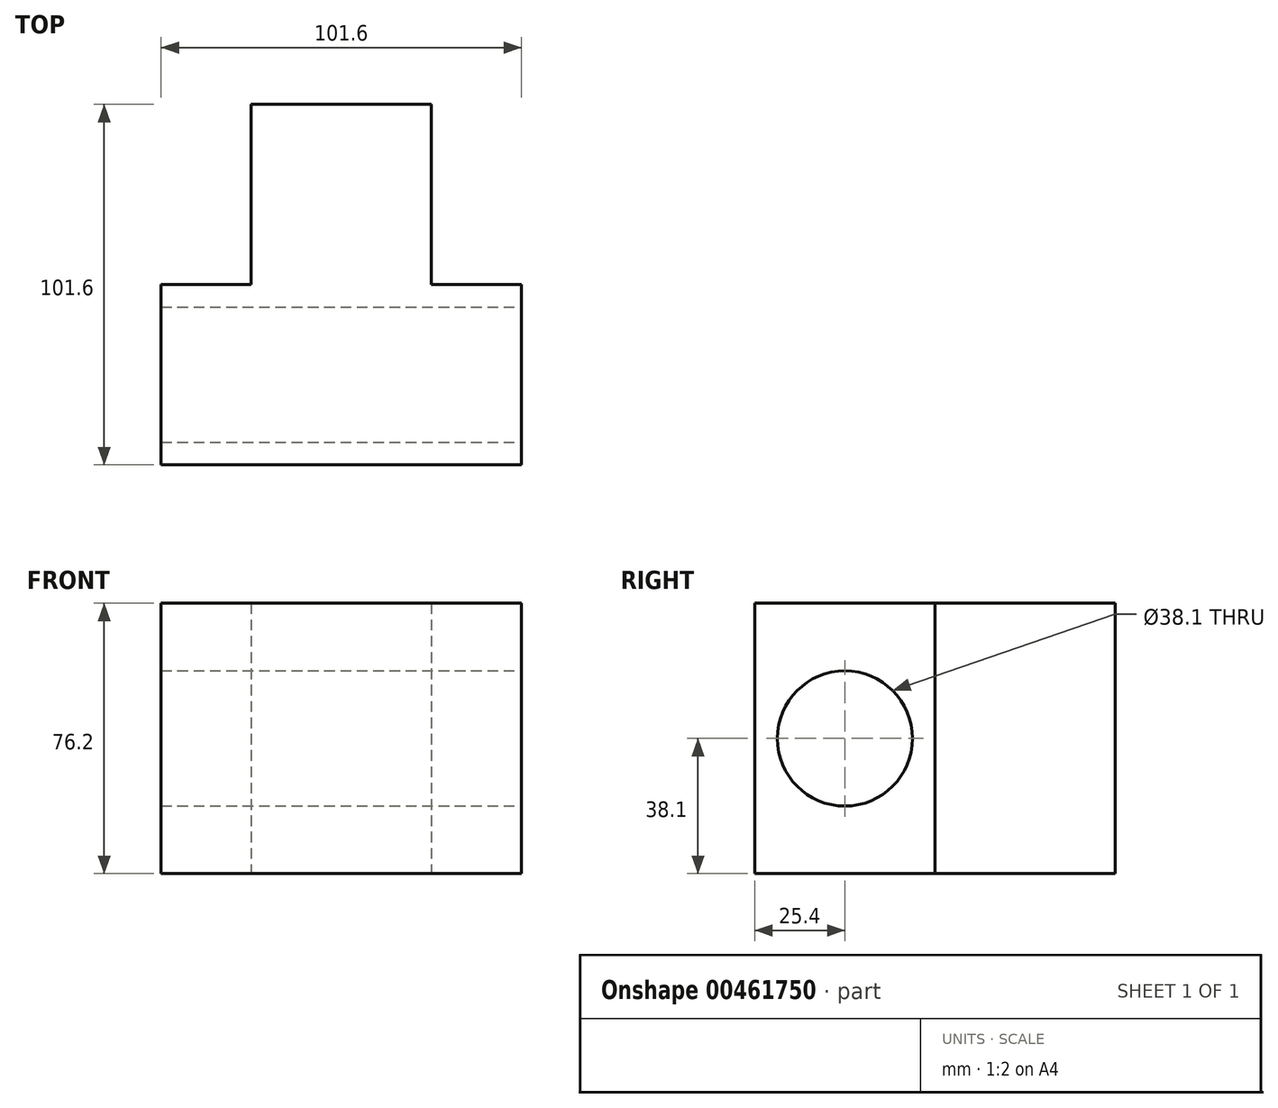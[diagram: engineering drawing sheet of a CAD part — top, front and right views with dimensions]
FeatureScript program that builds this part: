
annotation { "Feature Type Name" : "Feature", "Feature Type Description" : "" }
export const myFeature = defineFeature(function(context is Context, id is Id, definition is map)
    precondition{}
    {
        {
            var Q0;
            Q0=qCreatedBy(makeId("Top.planeOp"),FACE);
            var sketch = newSketch(context, id + "F0", { "sketchPlane" : qUnion([Q0])});
            skLineSegment(sketch, "E0.bottom", {"start": v(-50.8, -25.4) * mm, "end": v(50.8, -25.4) * mm});
            skLineSegment(sketch, "E0.top", {"start": v(-50.8, 25.4) * mm, "end": v(50.8, 25.4) * mm});
            skLineSegment(sketch, "E0.left", {"start": v(-50.8, -25.4) * mm, "end": v(-50.8, 25.4) * mm});
            skLineSegment(sketch, "E0.right", {"start": v(50.8, -25.4) * mm, "end": v(50.8, 25.4) * mm});
            skPoint(sketch, "E0.middle", {"position": v(0, 0) * mm});
            skLineSegment(sketch, "E1", {"start": v(0, 0) * mm, "end": v(0, 50.8) * mm});
            skLineSegment(sketch, "E2", {"start": v(0, 50.8) * mm, "end": v(0, 0) * mm});
            skLineSegment(sketch, "E3.bottom", {"start": v(-25.4, 25.4) * mm, "end": v(25.4, 25.4) * mm});
            skLineSegment(sketch, "E3.top", {"start": v(-25.4, 76.2) * mm, "end": v(25.4, 76.2) * mm});
            skLineSegment(sketch, "E3.left", {"start": v(-25.4, 25.4) * mm, "end": v(-25.4, 76.2) * mm});
            skLineSegment(sketch, "E3.right", {"start": v(25.4, 25.4) * mm, "end": v(25.4, 76.2) * mm});
            skPoint(sketch, "E3.middle", {"position": v(0, 50.8) * mm});
            skSolve(sketch);
        }
        {
            var Q0;
            Q0=makeQuery(id+"F0.imprint","IMPRINT",FACE,{"disambiguationData":[TD([[makeQuery(id+"F0.imprint","IMPRINT",EDGE,{"derivedFrom":sQuery(id+"F0.wireOp",EDGE,"E0.bottom")}),1.0]])]});
            var Q1;
            Q1=makeQuery(id+"F0.imprint","IMPRINT",FACE,{"disambiguationData":[TD([[makeQuery(id+"F0.imprint","IMPRINT",EDGE,{"derivedFrom":sQuery(id+"F0.wireOp",EDGE,"E3.top")}),-1.0]])]});
            extrude(context, id + "F1", {"entities" : qUnion([Q0, Q1]), "endBound" : BoundingType.SYMMETRIC, "depth" : 76.2 * mm});
        }
        {
            var Q0;
            Q0=makeQuery(id+"F1.opExtrude","SWEPT_FACE",FACE,{"disambiguationData":[OSD([sQuery(id+"F0.wireOp",EDGE,"E0.right")])]});
            var sketch = newSketch(context, id + "F2", { "sketchPlane" : qUnion([Q0])});
            skCircle(sketch, "E4", {"center": v(0, 0) * mm, "radius": 19.05 * mm});
            skSolve(sketch);
        }
        {
            var Q0;
            Q0=makeQuery(id+"F2.imprint","IMPRINT",FACE,{"disambiguationData":[TD([[makeQuery(id+"F2.imprint","IMPRINT",EDGE,{"derivedFrom":sQuery(id+"F2.wireOp",EDGE,"E4")}),1.0]])]});
            extrude(context, id + "F3", {"entities" : qUnion([Q0]), "operationType" : NewBodyOperationType.REMOVE, "endBound" : BoundingType.THROUGH_ALL, "oppositeDirection" : true, "depth" : 25.4 * mm});
        }
    });
